# Revit family: LTC-6RDW-W
name_source: partatom
category: Lighting Fixtures
revit_build: Autodesk Revit 2017 (Build: 20160225_1515(x64)
units: mm (PartAtom-declared; Revit-internal decimal feet)

## family parameters
Cut with Voids When Loaded = No
Host = Face
Light Source = Yes
OmniClass Number = 23.80.70.11.14.11
OmniClass Title = Downlights
Part Type = Normal
Room Calculation Point = No
Round Connector Dimension = Use Diameter
Shared = No

## types (2) — shared parameters
Apparent Load = 50 VA
Backbox = Hubbell - Matt Black
Ballast = Paint - Hubbell - Carbon Black
Certifications = • cCSAus certified to UL 1598
• Wall Mount: Suitable for wet locations
• Surface & Pendant Mount: Suitable for wet
locations under covered ceiling
• Cord Mount and all Wall Wash: Suitable for
damp locations
Color Filter = 16777215
Cord Height = 72 "
Default Elevation = 48 "
Description = LITEISTRY™ 6inch Round Cylinder with color turning
Dimming Lamp Color Temperature Shift = <None>
Emit Shape Visible in Rendering = No
Emit from Circle Diameter = 7.3 "
Features = • 6inch architectural LED downlight and wall wash cylinder delivering 600 - 2500 lm 
• 4 beam distributions from 0.3 to 1.1 Spacing Criteria 
• Quiet reflector appearance with 50º optical cutoff 
• SpectraSync™ Color Tuning technology allows the flexibility to tailor CCT to aesthetic preferences
• Available in Dim To Warm (2200K-3000K) or Tunable White (2700K-5000K or 2700K-6500K), 90+ CRI 
• Available in Surface, Wall, Pendant, or Cable/Cord Mount configurations 
• Versatile canopy options for recessed and surface-mounted J-box applications 
• Standard with 0-10V dimming to 5%
Lamp = LED Lamp
Manufacturer = Prescolite
Model = LTC-6RDW
Photometric Web File = LTC-6RD-P-20L35K8MD-DM1-S-BL (1).ies
Product Documentation Link = https://hubbellcdn.com
Product Page URL = https://www.hubbell.com
Reflector = Glass - Hubbell - Glass
Tilt Angle = -90.00°
URL = https://www.hubbell.com
Voltage = 120 V
Warranty = • 5 year warranty
• See HLI Standard Warranty for
additional information

## per-type parameters (varying)
| type | Canopy Height | Canopy Width | Center Distance |
| LTC-6RDW-W | 0.5 " | 4.5 " | 6.4 " |
| LTC-6RDW-WCC | 3 " | 5.74 " | 8.77 " |

## geometry (parser evidence)
native form markers: Blend x1, Sweep x2
no freeform markers — native parametric forms only
